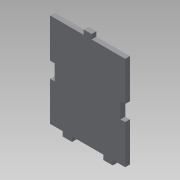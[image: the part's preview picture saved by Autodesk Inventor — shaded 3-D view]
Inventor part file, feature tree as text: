
AUTODESK INVENTOR PART (.ipt)
format: ipt  version: 2013 (Build 170138000, 138)  size: 106,496 bytes
history: native  units: mm
features: extrude x1
ambient origin geometry x8: Origin, YZ Plane, XZ Plane, XY Plane, X Axis, Y Axis, Z Axis, Center Point
bodies: Solid1 (feature_tree)
feature tree (1):
  extrude  "Extrusion1"  Depth=48.0mm
